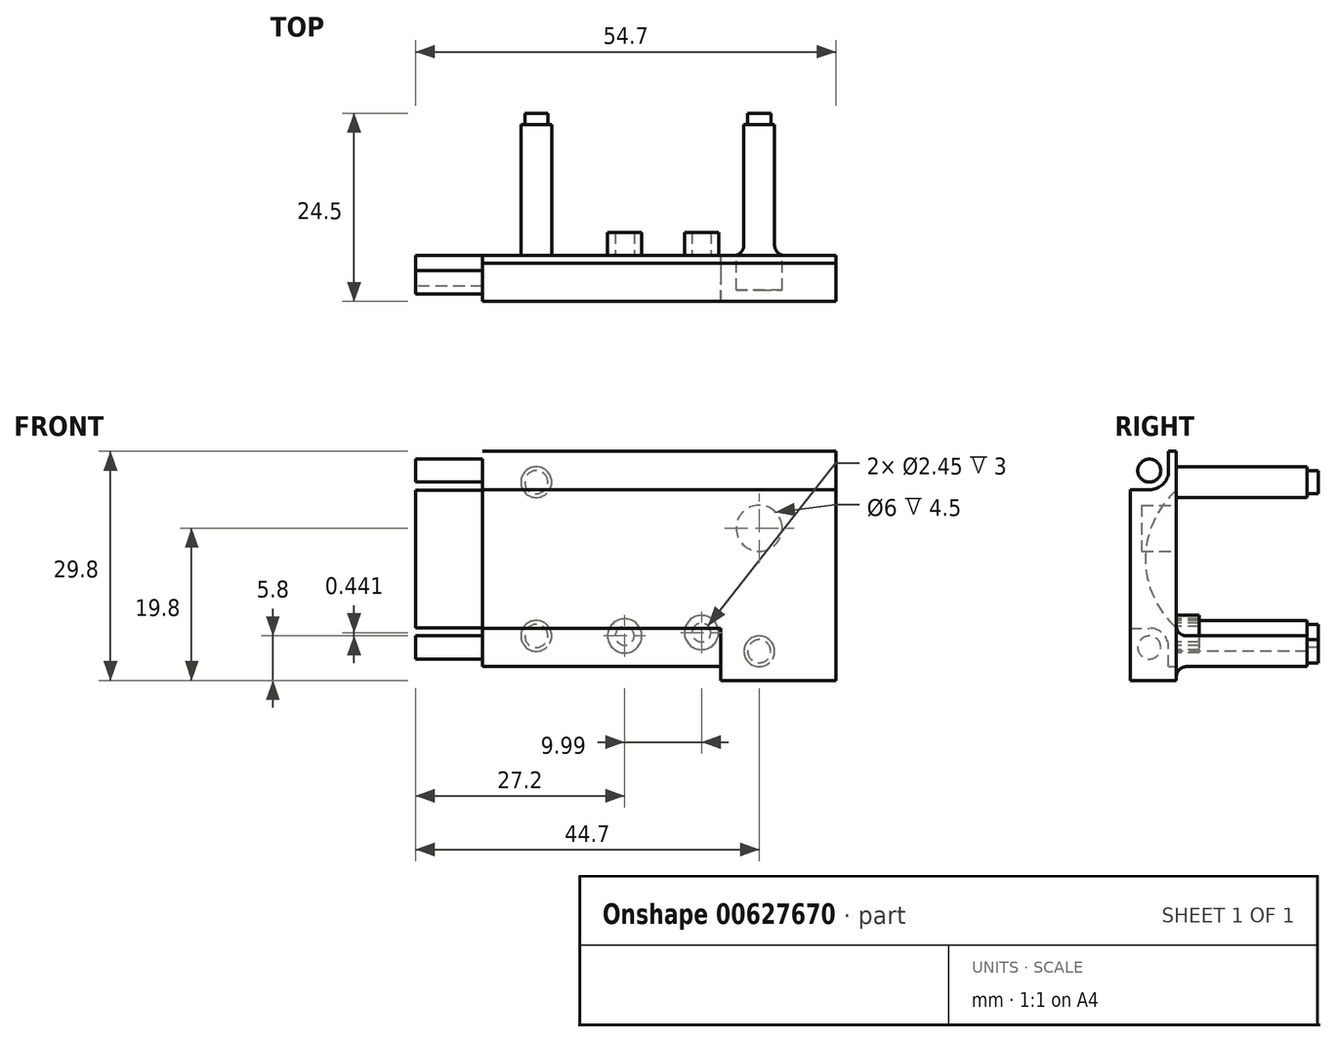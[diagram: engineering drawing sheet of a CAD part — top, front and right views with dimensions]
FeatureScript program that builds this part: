
annotation { "Feature Type Name" : "Feature", "Feature Type Description" : "" }
export const myFeature = defineFeature(function(context is Context, id is Id, definition is map)
    precondition{}
    {
        {
            var Q0;
            Q0=qCreatedBy(makeId("Front.planeOp"),FACE);
            var sketch = newSketch(context, id + "F0", { "sketchPlane" : qUnion([Q0])});
            skLineSegment(sketch, "E0.bottom", {"start": v(0, 0) * mm, "end": v(40, 0) * mm});
            skLineSegment(sketch, "E0.top", {"start": v(0, -28) * mm, "end": v(40, -28) * mm});
            skLineSegment(sketch, "E0.left", {"start": v(0, 0) * mm, "end": v(0, -28) * mm});
            skLineSegment(sketch, "E0.right", {"start": v(40, 0) * mm, "end": v(40, -28) * mm});
            skSolve(sketch);
        }
        {
            var Q0;
            Q0=makeQuery(id+"F0.imprint","IMPRINT",FACE,{"disambiguationData":[TD([[makeQuery(id+"F0.imprint","IMPRINT",EDGE,{"derivedFrom":sQuery(id+"F0.wireOp",EDGE,"E0.bottom")}),-1.0]])]});
            extrude(context, id + "F1", {"entities" : qUnion([Q0]), "depth" : 6 * mm, "offsetDistance" : 25 * mm});
        }
        {
            var Q0;
            Q0=makeQuery(id+"F1.opExtrude","SWEPT_FACE",FACE,{"disambiguationData":[OSD([sQuery(id+"F0.wireOp",EDGE,"E0.right")])]});
            var sketch = newSketch(context, id + "F2", { "sketchPlane" : qUnion([Q0])});
            skCircle(sketch, "E1", {"center": v(8, -14) * mm, "radius": 11 * mm, "construction": true});
            skPoint(sketch, "E1.centerSnap0", {"position": v(0, -14) * mm});
            skCircle(sketch, "E2", {"center": v(-3.5, -25.5) * mm, "radius": 1.5 * mm, "construction": true});
            skCircle(sketch, "E3", {"center": v(-3.5, -2.5) * mm, "radius": 1.5 * mm, "construction": true});
            skLineSegment(sketch, "E4.bottom", {"start": v(-6, -28) * mm, "end": v(-1, -28) * mm});
            skLineSegment(sketch, "E4.top", {"start": v(-6, -23) * mm, "end": v(-3.5, -23) * mm});
            skLineSegment(sketch, "E4.left", {"start": v(-6, -28) * mm, "end": v(-6, -23) * mm});
            skLineSegment(sketch, "E4.right", {"start": v(-1, -28) * mm, "end": v(-1, -25.5) * mm});
            skLineSegment(sketch, "E5.bottom", {"start": v(-6, 0) * mm, "end": v(-1, 0) * mm});
            skLineSegment(sketch, "E5.top", {"start": v(-6, -5) * mm, "end": v(-3.5, -5) * mm});
            skLineSegment(sketch, "E5.left", {"start": v(-6, 0) * mm, "end": v(-6, -5) * mm});
            skLineSegment(sketch, "E5.right", {"start": v(-1, 0) * mm, "end": v(-1, -2.5) * mm});
            skPoint(sketch, "E6.visualSharp", {"position": v(-1, -23) * mm});
            skArc(sketch, "E6.filletArc", {"start": v(-1, -25.5) * mm, "mid": v(-1.73, -23.73) * mm, "end": v(-3.5, -23) * mm});
            skPoint(sketch, "E7.visualSharp", {"position": v(-1, -5) * mm});
            skArc(sketch, "E7.filletArc", {"start": v(-3.5, -5) * mm, "mid": v(-1.73, -4.27) * mm, "end": v(-1, -2.5) * mm});
            skSolve(sketch);
        }
        {
            var Q0;
            Q0=makeQuery(id+"F2.imprint","IMPRINT",FACE,{"disambiguationData":[TD([[makeQuery(id+"F2.imprint","IMPRINT",EDGE,{"derivedFrom":sQuery(id+"F2.wireOp",EDGE,"E4.bottom")}),1.0]])]});
            var Q1;
            Q1=makeQuery(id+"F2.imprint","IMPRINT",FACE,{"disambiguationData":[TD([[makeQuery(id+"F2.imprint","IMPRINT",EDGE,{"derivedFrom":sQuery(id+"F2.wireOp",EDGE,"E5.bottom")}),-1.0]])]});
            var Q2;
            Q2=makeQuery(id+"F1.opExtrude","SWEPT_FACE",FACE,{"disambiguationData":[OSD([sQuery(id+"F0.wireOp",EDGE,"E0.left")])]});
            extrude(context, id + "F3", {"entities" : qUnion([Q0, Q1]), "operationType" : NewBodyOperationType.REMOVE, "endBound" : BoundingType.UP_TO_SURFACE, "oppositeDirection" : true, "depth" : 25 * mm, "endBoundEntityFace" : qUnion([Q2]), "hasOffset" : true, "offsetDistance" : 2 * mm});
        }
        {
            var Q0;
            Q0=makeQuery(id+"F1.opExtrude","SWEPT_FACE",FACE,{"disambiguationData":[OSD([sQuery(id+"F0.wireOp",EDGE,"E0.left")])]});
            var sketch = newSketch(context, id + "F4", { "sketchPlane" : qUnion([Q0])});
            skCircle(sketch, "E8.0", {"center": v(3.5, -2.5) * mm, "radius": 1.5 * mm});
            skCircle(sketch, "E8.1", {"center": v(3.5, -25.5) * mm, "radius": 1.5 * mm});
            skArc(sketch, "E9.0", {"start": v(0, -5.06) * mm, "mid": v(4, -14) * mm, "end": v(0, -22.94) * mm});
            skLineSegment(sketch, "E10", {"start": v(0, -5.06) * mm, "end": v(0, -22.94) * mm});
            skSolve(sketch);
        }
        {
            var Q0;
            Q0=makeQuery(id+"F4.imprint","IMPRINT",FACE,{"disambiguationData":[TD([[makeQuery(id+"F4.imprint","IMPRINT",EDGE,{"derivedFrom":sQuery(id+"F4.wireOp",EDGE,"E8.1")}),-1.0]])]});
            var Q1;
            Q1=makeQuery(id+"F4.imprint","IMPRINT",FACE,{"disambiguationData":[TD([[makeQuery(id+"F4.imprint","IMPRINT",EDGE,{"derivedFrom":sQuery(id+"F4.wireOp",EDGE,"E9.0")}),-1.0]])]});
            var Q2;
            Q2=makeQuery(id+"F4.imprint","IMPRINT",FACE,{"disambiguationData":[TD([[makeQuery(id+"F4.imprint","IMPRINT",EDGE,{"derivedFrom":sQuery(id+"F4.wireOp",EDGE,"E8.0")}),-1.0]])]});
            extrude(context, id + "F5", {"entities" : qUnion([Q0, Q1, Q2]), "operationType" : NewBodyOperationType.REMOVE, "oppositeDirection" : true, "depth" : 2 * mm, "offsetDistance" : 25 * mm});
        }
        {
            var Q0;
            Q0=makeQuery(id+"F1.opExtrude","CAP_FACE",FACE,{"disambiguationData":[OSD([sQuery(id+"F0.wireOp",EDGE,"E0.bottom"),sQuery(id+"F0.wireOp",EDGE,"E0.top"),sQuery(id+"F0.wireOp",EDGE,"E0.left"),sQuery(id+"F0.wireOp",EDGE,"E0.right")])],"isStart":true});
            var sketch = newSketch(context, id + "F6", { "sketchPlane" : qUnion([Q0])});
            skCircle(sketch, "E11", {"center": v(-20.5, -24) * mm, "radius": 7.5 * mm, "construction": true});
            skCircle(sketch, "E12", {"center": v(-30.5, -23.56) * mm, "radius": 2.5 * mm, "construction": true});
            skCircle(sketch, "E13", {"center": v(-30.5, -23.56) * mm, "radius": 5 * mm, "construction": true});
            skCircle(sketch, "E14", {"center": v(-38, -10) * mm, "radius": 10.5 * mm, "construction": true});
            skCircle(sketch, "E15", {"center": v(-38, -26) * mm, "radius": 2 * mm, "construction": true});
            skCircle(sketch, "E16", {"center": v(-20.5, -24) * mm, "radius": 5 * mm, "construction": true});
            skSolve(sketch);
        }
        {
            var Q0;
            {var subQ6=sQuery(id+"F0.wireOp",EDGE,"E0.bottom");Q0=makeQuery(id+"F6.imprint","IMPRINT",FACE,{"disambiguationData":[TD([[makeQuery(id+"F6.imprint","IMPRINT",EDGE,{"derivedFrom":makeQuery(id+"F1.opExtrude","CAP_EDGE",EDGE,{"disambiguationData":[OSD([subQ6])],"isStart":true})}),1.0]])]});}
            var sketch = newSketch(context, id + "F7", { "sketchPlane" : qUnion([Q0])});
            skPoint(sketch, "E17.0", {"position": v(-20.5, -24) * mm});
            skPoint(sketch, "E17.1", {"position": v(-30.5, -23.56) * mm});
            skCircle(sketch, "E18", {"center": v(-20.5, -24) * mm, "radius": 1.23 * mm});
            skCircle(sketch, "E19", {"center": v(-30.5, -23.56) * mm, "radius": 1.23 * mm});
            skCircle(sketch, "E20.0", {"center": v(-20.5, -24) * mm, "radius": 2.23 * mm});
            skCircle(sketch, "E21.0", {"center": v(-30.5, -23.56) * mm, "radius": 2.23 * mm});
            skSolve(sketch);
        }
        {
            var Q0;
            Q0 = qSketchRegion(id + "F7", true);
            extrude(context, id + "F8", {"entities" : qUnion([Q0]), "operationType" : NewBodyOperationType.ADD, "depth" : 3 * mm, "offsetDistance" : 25 * mm});
        }
        {
            var Q0;
            {var subQ6=sQuery(id+"F0.wireOp",EDGE,"E0.bottom");Q0=makeQuery(id+"F6.imprint","IMPRINT",FACE,{"disambiguationData":[TD([[makeQuery(id+"F6.imprint","IMPRINT",EDGE,{"derivedFrom":makeQuery(id+"F1.opExtrude","CAP_EDGE",EDGE,{"disambiguationData":[OSD([subQ6])],"isStart":true})}),1.0]])]});}
            var sketch = newSketch(context, id + "F9", { "sketchPlane" : qUnion([Q0])});
            skCircle(sketch, "E22.0", {"center": v(-38, -26) * mm, "radius": 2 * mm});
            skCircle(sketch, "E23", {"center": v(-9, -24) * mm, "radius": 2 * mm});
            skCircle(sketch, "E24", {"center": v(-9, -4) * mm, "radius": 2 * mm});
            skSolve(sketch);
        }
        {
            var Q0;
            Q0 = qSketchRegion(id + "F9", true);
            extrude(context, id + "F10", {"entities" : qUnion([Q0]), "operationType" : NewBodyOperationType.ADD, "depth" : 17 * mm, "offsetDistance" : 25 * mm});
        }
        {
            var Q0;
            Q0=makeQuery(id+"F10.opExtrude","CAP_FACE",FACE,{"disambiguationData":[OSD([sQuery(id+"F9.wireOp",EDGE,"E22.0")])],"isStart":false});
            var sketch = newSketch(context, id + "F11", { "sketchPlane" : qUnion([Q0])});
            skCircle(sketch, "E25.0", {"center": v(-38, -26) * mm, "radius": 1.5 * mm});
            skCircle(sketch, "E26.0", {"center": v(-9, -24) * mm, "radius": 1.5 * mm});
            skCircle(sketch, "E27.0", {"center": v(-9, -4) * mm, "radius": 1.5 * mm});
            skSolve(sketch);
        }
        {
            var Q0;
            Q0 = qSketchRegion(id + "F11", true);
            extrude(context, id + "F12", {"entities" : qUnion([Q0]), "operationType" : NewBodyOperationType.ADD, "depth" : 1.5 * mm, "offsetDistance" : 25 * mm});
        }
        {
            var Q0;
            Q0=makeQuery(id+"F1.opExtrude","SWEPT_FACE",FACE,{"disambiguationData":[OSD([sQuery(id+"F0.wireOp",EDGE,"E0.left")])]});
            extrude(context, id + "F13", {"entities" : qUnion([Q0]), "operationType" : NewBodyOperationType.ADD, "depth" : 6.7 * mm, "offsetDistance" : 25 * mm});
        }
        {
            var Q0;
            Q0=makeQuery(id+"F1.opExtrude","SWEPT_FACE",FACE,{"disambiguationData":[OSD([sQuery(id+"F0.wireOp",EDGE,"E0.right")])]});
            var sketch = newSketch(context, id + "F14", { "sketchPlane" : qUnion([Q0])});
            skLineSegment(sketch, "E28.0", {"start": v(-1, 0) * mm, "end": v(-1, -2.5) * mm});
            skArc(sketch, "E28.1", {"start": v(-3.5, -5) * mm, "mid": v(-1.73, -4.27) * mm, "end": v(-1, -2.5) * mm});
            skLineSegment(sketch, "E28.2", {"start": v(-1, 0) * mm, "end": v(0, 0) * mm});
            skLineSegment(sketch, "E28.3", {"start": v(-6, -5) * mm, "end": v(-3.5, -5) * mm});
            skLineSegment(sketch, "E28.4", {"start": v(-6, -5) * mm, "end": v(-6, -23) * mm});
            skLineSegment(sketch, "E28.5", {"start": v(-6, -23) * mm, "end": v(-3.5, -23) * mm});
            skArc(sketch, "E28.6", {"start": v(-1, -25.5) * mm, "mid": v(-1.73, -23.73) * mm, "end": v(-3.5, -23) * mm});
            skLineSegment(sketch, "E28.7", {"start": v(-1, -28) * mm, "end": v(-1, -25.5) * mm});
            skLineSegment(sketch, "E28.8", {"start": v(-1, -28) * mm, "end": v(0, -28) * mm});
            skLineSegment(sketch, "E29", {"start": v(0, -28) * mm, "end": v(0, 0) * mm});
            skSolve(sketch);
        }
        {
            var Q0;
            Q0 = qSketchRegion(id + "F14", true);
            extrude(context, id + "F15", {"entities" : qUnion([Q0]), "operationType" : NewBodyOperationType.ADD, "depth" : 8 * mm, "offsetDistance" : 25 * mm});
        }
        {
            var Q0;
            {var subQ6=sQuery(id+"F0.wireOp",EDGE,"E0.bottom");Q0=makeQuery(id+"F6.imprint","IMPRINT",FACE,{"disambiguationData":[TD([[makeQuery(id+"F6.imprint","IMPRINT",EDGE,{"derivedFrom":makeQuery(id+"F1.opExtrude","CAP_EDGE",EDGE,{"disambiguationData":[OSD([subQ6])],"isStart":true})}),1.0]])]});}
            var sketch = newSketch(context, id + "F16", { "sketchPlane" : qUnion([Q0])});
            skPoint(sketch, "E30.0", {"position": v(-38, -10) * mm});
            skCircle(sketch, "E31", {"center": v(-38, -10) * mm, "radius": 3 * mm});
            skSolve(sketch);
        }
        {
            var Q0;
            Q0 = qSketchRegion(id + "F16", true);
            extrude(context, id + "F17", {"entities" : qUnion([Q0]), "operationType" : NewBodyOperationType.REMOVE, "oppositeDirection" : true, "depth" : 4.5 * mm, "offsetDistance" : 25 * mm});
        }
        {
            var Q0;
            Q0=makeQuery(id+"F15.opExtrude","CAP_FACE",FACE,{"disambiguationData":[OSD([sQuery(id+"F14.wireOp",EDGE,"E28.0"),sQuery(id+"F14.wireOp",EDGE,"E28.1"),sQuery(id+"F14.wireOp",EDGE,"E28.2"),sQuery(id+"F14.wireOp",EDGE,"E28.3"),sQuery(id+"F14.wireOp",EDGE,"E28.4"),sQuery(id+"F14.wireOp",EDGE,"E28.5"),sQuery(id+"F14.wireOp",EDGE,"E28.6"),sQuery(id+"F14.wireOp",EDGE,"E28.7"),sQuery(id+"F14.wireOp",EDGE,"E28.8"),sQuery(id+"F14.wireOp",EDGE,"E29")])],"isStart":false});
            var sketch = newSketch(context, id + "F18", { "sketchPlane" : qUnion([Q0])});
            skLineSegment(sketch, "E32.0", {"start": v(-6, -23) * mm, "end": v(-3.5, -23) * mm});
            skArc(sketch, "E32.1", {"start": v(-1, -25.5) * mm, "mid": v(-1.73, -23.73) * mm, "end": v(-3.5, -23) * mm});
            skLineSegment(sketch, "E32.2", {"start": v(-1, -28) * mm, "end": v(-1, -25.5) * mm});
            skLineSegment(sketch, "E32.3", {"start": v(-1, -28) * mm, "end": v(0, -28) * mm});
            skLineSegment(sketch, "E33", {"start": v(0, -28) * mm, "end": v(0, -29.8) * mm});
            skLineSegment(sketch, "E34", {"start": v(0, -29.8) * mm, "end": v(-6, -29.8) * mm});
            skLineSegment(sketch, "E35", {"start": v(-6, -29.8) * mm, "end": v(-6, -23) * mm});
            skSolve(sketch);
        }
        {
            var Q0;
            Q0=makeQuery(id+"F18.imprint","IMPRINT",FACE,{"disambiguationData":[TD([[makeQuery(id+"F18.imprint","IMPRINT",EDGE,{"derivedFrom":sQuery(id+"F18.wireOp",EDGE,"E32.0")}),-1.0]])]});
            extrude(context, id + "F19", {"entities" : qUnion([Q0]), "operationType" : NewBodyOperationType.ADD, "oppositeDirection" : true, "depth" : 15 * mm, "offsetDistance" : 25 * mm});
        }
        {
            var Q0;
            {var subQ0=makeQuery(id+"F10.opExtrude","CAP_EDGE",EDGE,{"disambiguationData":[OSD([sQuery(id+"F9.wireOp",EDGE,"E22.0")])],"isStart":true});Q0=makeQuery(id+"F15.boolean.opBoolean","MERGE",EDGE,{"derivedFrom":[makeQuery(id+"F10.boolean.opBoolean","SPLIT",EDGE,{"disambiguationData":[OD(0.0)],"derivedFrom":subQ0}),makeQuery(id+"F10.boolean.opBoolean","SPLIT",EDGE,{"disambiguationData":[OD(1.0)],"derivedFrom":subQ0})]});}
            var Q1;
            Q1=makeQuery(id+"F10.opExtrude","CAP_EDGE",EDGE,{"disambiguationData":[OSD([sQuery(id+"F9.wireOp",EDGE,"E23")])],"isStart":true});
            var Q2;
            Q2=makeQuery(id+"F10.opExtrude","CAP_EDGE",EDGE,{"disambiguationData":[OSD([sQuery(id+"F9.wireOp",EDGE,"E24")])],"isStart":true});
            fillet(context, id + "F20", {"entities" : qUnion([Q0, Q1, Q2]), "radius" : (4 / 3) * mm, "tangentPropagation" : true, "allowEdgeOverflow" : false});
        }
    });
